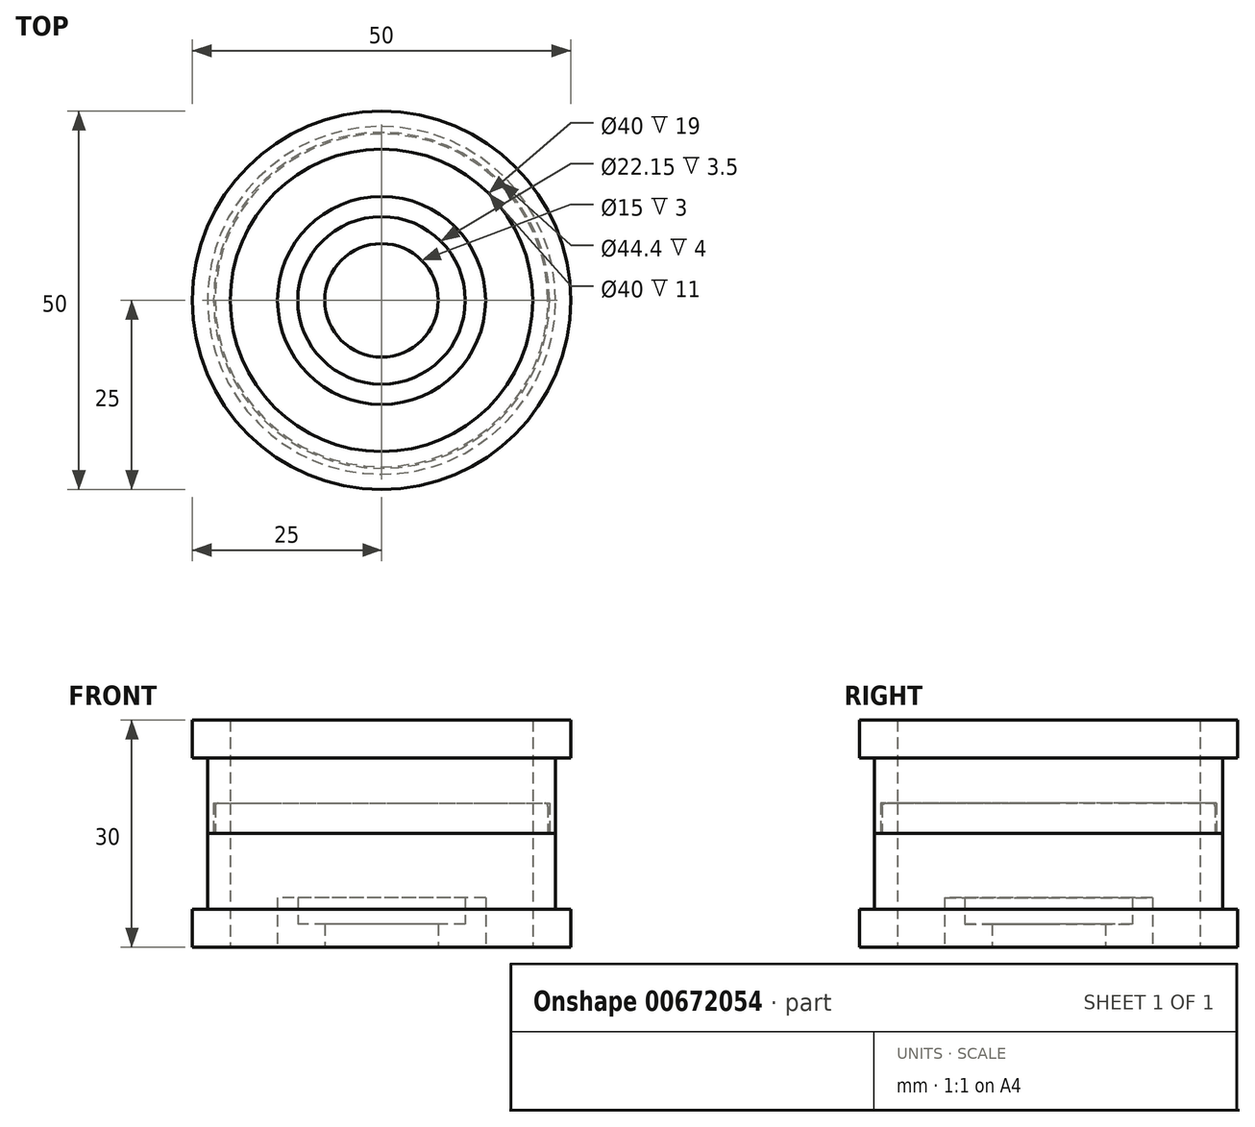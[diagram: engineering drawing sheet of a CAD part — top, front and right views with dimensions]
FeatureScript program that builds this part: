
annotation { "Feature Type Name" : "Feature", "Feature Type Description" : "" }
export const myFeature = defineFeature(function(context is Context, id is Id, definition is map)
    precondition{}
    {
        {
            var Q0;
            Q0=qCreatedBy(makeId("Top.planeOp"),FACE);
            var sketch = newSketch(context, id + "F0", { "sketchPlane" : qUnion([Q0])});
            skCircle(sketch, "E0", {"center": v(0, 0) * mm, "radius": 11.07 * mm});
            skCircle(sketch, "E1", {"center": v(0, 0) * mm, "radius": 13.75 * mm});
            skCircle(sketch, "E2", {"center": v(0, 0) * mm, "radius": 20 * mm});
            skCircle(sketch, "E3", {"center": v(0, 0) * mm, "radius": 25 * mm});
            skCircle(sketch, "E4", {"center": v(0, 0) * mm, "radius": 7.5 * mm});
            skSolve(sketch);
        }
        {
            var Q0;
            Q0=qCreatedBy(makeId("Front.planeOp"),FACE);
            var sketch = newSketch(context, id + "F1", { "sketchPlane" : qUnion([Q0])});
            skPoint(sketch, "E5.0", {"position": v(0, 0) * mm});
            skLineSegment(sketch, "E6", {"start": v(20, 30) * mm, "end": v(20, 0) * mm, "construction": true});
            skLineSegment(sketch, "E7", {"start": v(25, 30) * mm, "end": v(25, 0) * mm, "construction": true});
            skLineSegment(sketch, "E8", {"start": v(25, 30) * mm, "end": v(25, 25) * mm});
            skLineSegment(sketch, "E9", {"start": v(25, 25) * mm, "end": v(23, 25) * mm});
            skLineSegment(sketch, "E10", {"start": v(23, 25) * mm, "end": v(23, 15) * mm});
            skLineSegment(sketch, "E11", {"start": v(25, 30) * mm, "end": v(20, 30) * mm});
            skLineSegment(sketch, "E12", {"start": v(20, 15) * mm, "end": v(20, 30) * mm});
            skLineSegment(sketch, "E13", {"start": v(20, 15) * mm, "end": v(23, 15) * mm});
            skLineSegment(sketch, "E14.MirrorCS", {"start": v(23, 5) * mm, "end": v(23, 15) * mm});
            skLineSegment(sketch, "E15.MirrorCS", {"start": v(25, 0) * mm, "end": v(25, 5) * mm});
            skLineSegment(sketch, "E16.MirrorCS", {"start": v(25, 5) * mm, "end": v(23, 5) * mm});
            skLineSegment(sketch, "E17.MirrorCS", {"start": v(25, 0) * mm, "end": v(20, 0) * mm});
            skLineSegment(sketch, "E18.MirrorCS", {"start": v(20, 15) * mm, "end": v(20, 0) * mm});
            skLineSegment(sketch, "E19", {"start": v(25, 25) * mm, "end": v(25, 5) * mm});
            skSolve(sketch);
        }
        {
            var Q0;
            Q0=makeQuery(id+"F0.imprint","IMPRINT",FACE,{"disambiguationData":[TD([[makeQuery(id+"F0.imprint","IMPRINT",EDGE,{"derivedFrom":sQuery(id+"F0.wireOp",EDGE,"E0")}),-1.0]])]});
            extrude(context, id + "F2", {"entities" : qUnion([Q0]), "depth" : 6.5 * mm, "offsetDistance" : 25 * mm});
        }
        {
            var Q0;
            Q0=makeQuery(id+"F0.imprint","IMPRINT",FACE,{"disambiguationData":[TD([[makeQuery(id+"F0.imprint","IMPRINT",EDGE,{"derivedFrom":sQuery(id+"F0.wireOp",EDGE,"E0")}),1.0]])]});
            extrude(context, id + "F3", {"entities" : qUnion([Q0]), "operationType" : NewBodyOperationType.ADD, "depth" : 3 * mm, "offsetDistance" : 25 * mm});
        }
        {
            var Q0;
            Q0=qCreatedBy(makeId("Front.planeOp"),FACE);
            var sketch = newSketch(context, id + "F4", { "sketchPlane" : qUnion([Q0])});
            skLineSegment(sketch, "E20.0.0", {"start": v(23, 15) * mm, "end": v(20, 15) * mm});
            skLineSegment(sketch, "E20.0.1", {"start": v(20, 15) * mm, "end": v(20, 0) * mm});
            skLineSegment(sketch, "E20.0.2", {"start": v(20, 0) * mm, "end": v(25, 0) * mm});
            skLineSegment(sketch, "E20.0.3", {"start": v(25, 0) * mm, "end": v(25, 5) * mm});
            skLineSegment(sketch, "E20.0.4", {"start": v(25, 5) * mm, "end": v(23, 5) * mm});
            skLineSegment(sketch, "E20.0.5", {"start": v(23, 5) * mm, "end": v(23, 15) * mm});
            skLineSegment(sketch, "E21", {"start": v(20, 15) * mm, "end": v(20, 19) * mm});
            skLineSegment(sketch, "E22", {"start": v(20, 19) * mm, "end": v(22, 19) * mm});
            skLineSegment(sketch, "E23", {"start": v(22, 19) * mm, "end": v(22, 15) * mm});
            skSolve(sketch);
        }
        {
            var Q0;
            Q0=qCreatedBy(makeId("Front.planeOp"),FACE);
            var sketch = newSketch(context, id + "F5", { "sketchPlane" : qUnion([Q0])});
            skLineSegment(sketch, "E24.0.0", {"start": v(20, 30) * mm, "end": v(20, 15) * mm});
            skLineSegment(sketch, "E24.0.1", {"start": v(20, 15) * mm, "end": v(23, 15) * mm});
            skLineSegment(sketch, "E24.0.2", {"start": v(23, 15) * mm, "end": v(23, 25) * mm});
            skLineSegment(sketch, "E24.0.3", {"start": v(23, 25) * mm, "end": v(25, 25) * mm});
            skLineSegment(sketch, "E24.0.4", {"start": v(25, 25) * mm, "end": v(25, 30) * mm});
            skLineSegment(sketch, "E24.0.5", {"start": v(25, 30) * mm, "end": v(20, 30) * mm});
            skLineSegment(sketch, "E25.0", {"start": v(22.2, 19) * mm, "end": v(22.2, 15) * mm});
            skLineSegment(sketch, "E26.0", {"start": v(20, 19) * mm, "end": v(22, 19) * mm, "construction": true});
            skLineSegment(sketch, "E27", {"start": v(20, 19) * mm, "end": v(22.2, 19) * mm});
            skSolve(sketch);
        }
        {
            var Q0;
            {var subQ0=sQuery(id+"F4.wireOp",EDGE,"E20.0.1");Q0=makeQuery(id+"F4.imprint","IMPRINT",FACE,{"disambiguationData":[TD([[makeQuery(id+"F4.imprint","IMPRINT",EDGE,{"derivedFrom":subQ0}),1.0]])]});}
            var Q1;
            {var subQ0=sQuery(id+"F4.wireOp",EDGE,"E21");Q1=makeQuery(id+"F4.imprint","IMPRINT",FACE,{"disambiguationData":[TD([[makeQuery(id+"F4.imprint","IMPRINT",EDGE,{"derivedFrom":subQ0}),-1.0]])]});}
            var Q2;
            Q2=makeQuery(id+"F3.opExtrude","SWEPT_FACE",FACE,{"disambiguationData":[OSD([sQuery(id+"F0.wireOp",EDGE,"E4")])]});
            revolve(context, id + "F6", {"entities" : qUnion([Q0, Q1]), "axis" : qUnion([Q2]), "revolveType" : RevolveType.FULL});
        }
        {
            var Q0;
            {var subQ0=sQuery(id+"F5.wireOp",EDGE,"E24.0.2");Q0=makeQuery(id+"F5.imprint","IMPRINT",FACE,{"disambiguationData":[TD([[makeQuery(id+"F5.imprint","IMPRINT",EDGE,{"derivedFrom":subQ0}),1.0]])]});}
            var Q1;
            Q1=makeQuery(id+"F3.opExtrude","SWEPT_FACE",FACE,{"disambiguationData":[OSD([sQuery(id+"F0.wireOp",EDGE,"E4")])]});
            revolve(context, id + "F7", {"entities" : qUnion([Q0]), "axis" : qUnion([Q1]), "revolveType" : RevolveType.FULL});
        }
        {
            var Q0;
            Q0=makeQuery(id+"F6.opRevolve","SWEPT_EDGE",EDGE,{"disambiguationData":[OSD([sQuery(id+"F4.wireOp",EDGE,"E22"),sQuery(id+"F4.wireOp",EDGE,"E23")])]});
            fillet(context, id + "F8", {"entities" : qUnion([Q0]), "radius" : .4 * mm, "tangentPropagation" : true, "allowEdgeOverflow" : false});
        }
    });
